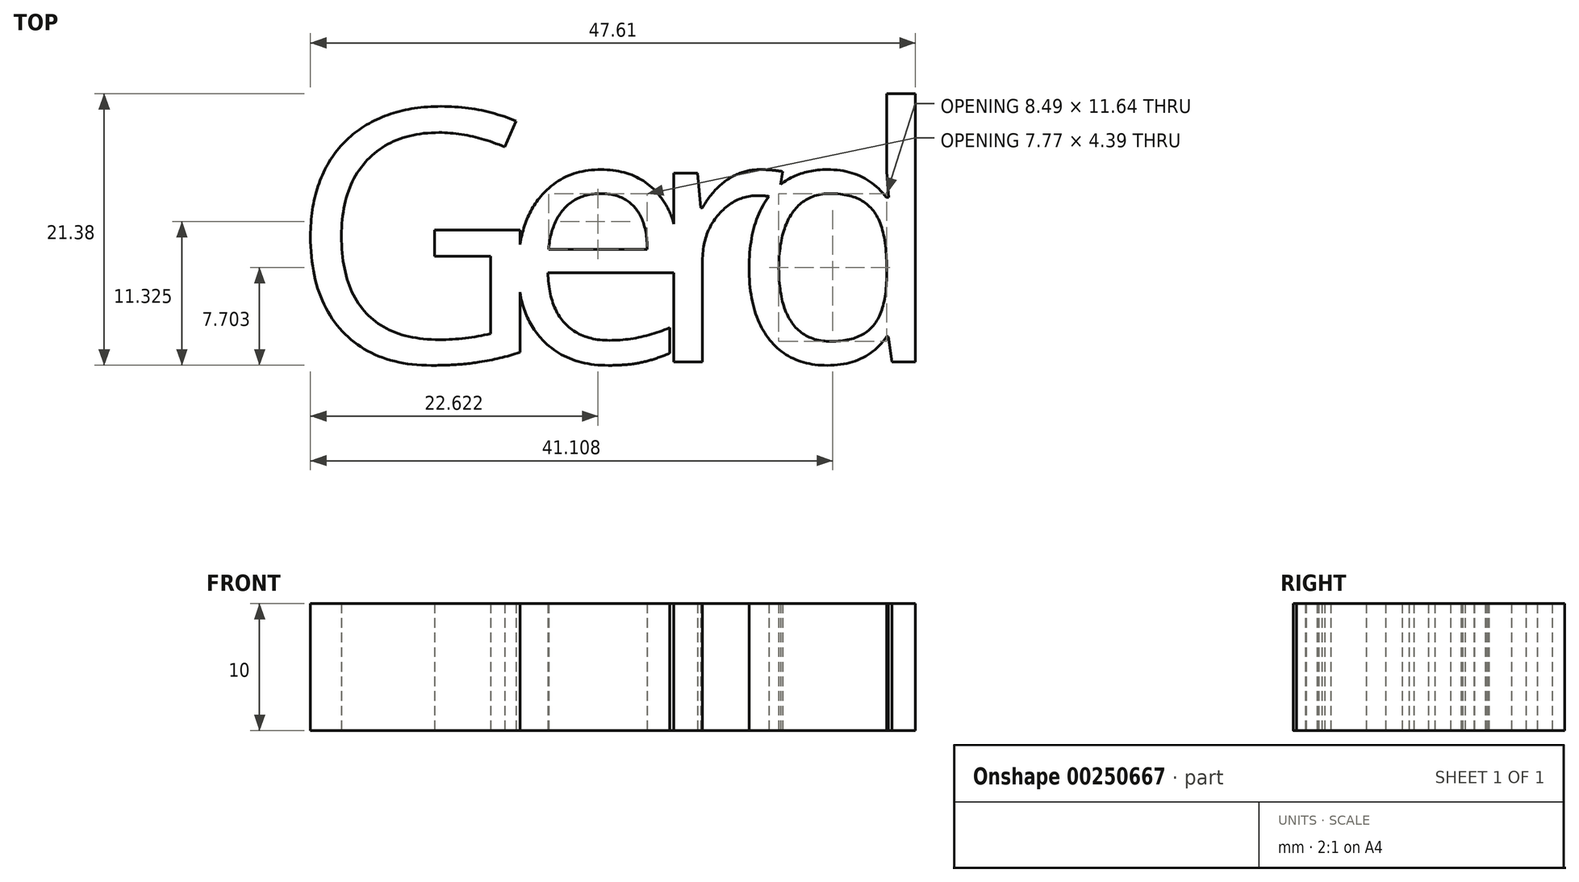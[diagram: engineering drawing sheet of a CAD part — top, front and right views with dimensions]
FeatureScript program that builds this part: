
annotation { "Feature Type Name" : "Feature", "Feature Type Description" : "" }
export const myFeature = defineFeature(function(context is Context, id is Id, definition is map)
    precondition{}
    {
        {
            var Q0;
            Q0=qCreatedBy(makeId("Top.planeOp"),FACE);
            var sketch = newSketch(context, id + "F0", { "sketchPlane" : qUnion([Q0])});
            skText(sketch, "E0", { "text": "G", "fontName": "OpenSans-Regular.ttf"});
            skText(sketch, "E1", { "text": "e", "fontName": "OpenSans-Regular.ttf"});
            skText(sketch, "E2", { "text": "r", "fontName": "OpenSans-Regular.ttf"});
            skText(sketch, "E3", { "text": "d", "fontName": "OpenSans-Regular.ttf"});
            const initialGuessF0  = {"E0": [-0.03745, 0, 1, 0, 0.02], "E1": [-0.02096, 0, 1, 0, 0.02], "E2": [-0.00953, 0, 1, 0, 0.02], "E3": [-0.00278, 0, 1, 0, 0.02]};
            skSetInitialGuess(sketch, initialGuessF0);
            skSolve(sketch);
        }
        {
            var Q0;
            Q0 = qSketchRegion(id + "F0", true);
            extrude(context, id + "F1", {"entities" : qUnion([Q0]), "depth" : 10 * mm});
        }
    });
